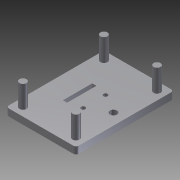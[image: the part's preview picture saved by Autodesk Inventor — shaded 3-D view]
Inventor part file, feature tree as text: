
AUTODESK INVENTOR PART (.ipt)
format: ipt  version: 2011 (Build 150239000, 239)  size: 134,656 bytes
history: native  units: mm
features: extrude x4, sketch x4, fillet x1
ambient origin geometry x8: Origin, YZ Plane, XZ Plane, XY Plane, X Axis, Y Axis, Z Axis, Center Point
bodies: Volumenkörper1 (feature_tree)
feature tree (9):
  extrude  "Extrusion1"  Depth=70.0mm
  fillet  "Rundung1"  Radius=5.0mm
  extrude  "Extrusion2"  Depth=3.0mm
  sketch  "Skizze3"  dims[d6=21.0mm d7=10.0mm d8=0.0mm]
  extrude  "Extrusion3"  Depth=10.0mm TaperAngle=0.0deg
  extrude  "Extrusion4"  Depth=21.0mm
  sketch  "Skizze1"  dims[d0=50.0mm d1=70.0mm d2=5.0mm d3=0.0mm]
  sketch  "Skizze2"  dims[d4=2.0mm d5=3.0mm]
  sketch  "Skizze4"  dims[d9=14.5mm d10=21.0mm d11=3.0mm d12=3.0mm d13=2.5mm d14=2.5mm d15=2.5mm d16=2.5mm d17=5.0mm d18=5.0mm d19=5.0mm d20=5.0mm d21=5.0mm d22=6.0mm d23=6.0mm d24=6.0mm d25=6.0mm d26=6.0mm d27=6.0mm d28=6.0mm d29=6.0mm d30=5.0mm d31=5.0mm d32=5.0mm d33=5.0mm d34=16.0mm d35=0.0mm d36=10.0mm d37=0.0mm]
